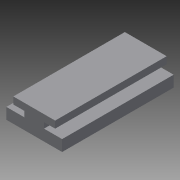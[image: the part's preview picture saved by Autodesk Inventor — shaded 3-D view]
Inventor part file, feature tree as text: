
AUTODESK INVENTOR PART (.ipt)
format: ipt  version: 2014 (Build 180170000, 170)  size: 80,896 bytes
history: native  units: in
note: dims shown in document units (in); Inventor stores cm internally (conversion verified against a paired STEP export)
features: extrude x1, sketch x1
ambient origin geometry x8: Origin, YZ Plane, XZ Plane, XY Plane, X Axis, Y Axis, Z Axis, Center Point
bodies: Body1 (feature_tree)
feature tree (2):
  extrude  "Extrusion2"  [1 undecoded]
  sketch  "Sketch1"  dims[d14=2.0in d15=0.0in]
note: 1 required parameter value undecoded (feature->parameter linkage not recoverable at this tier; creation-order binding heuristic only, values carry confidence <= 0.55)
